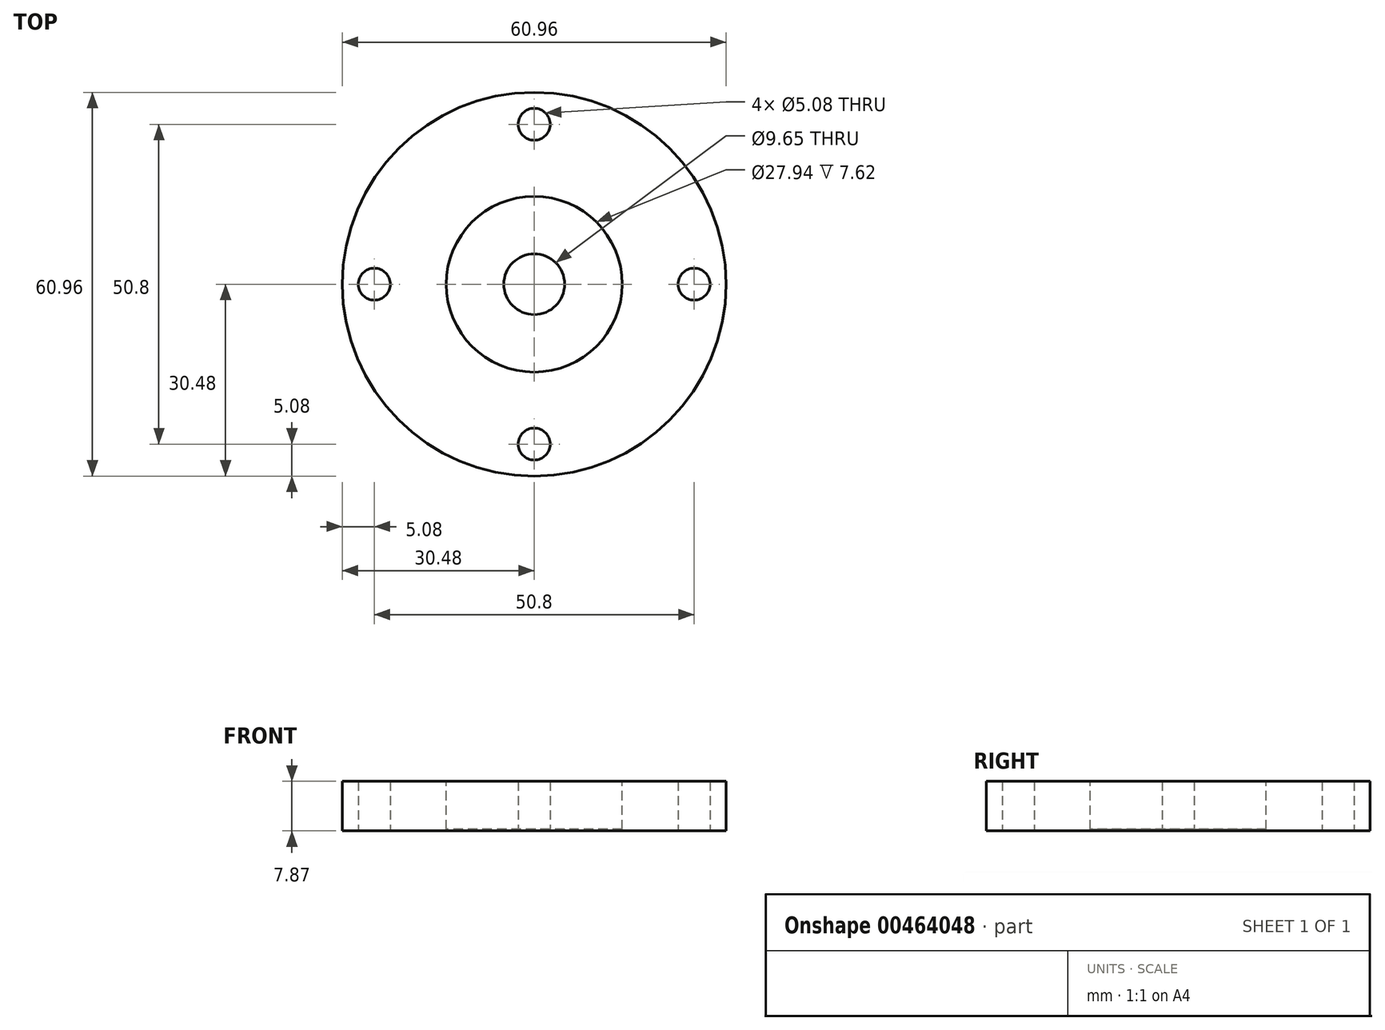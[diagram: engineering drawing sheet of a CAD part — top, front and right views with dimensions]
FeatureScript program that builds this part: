
annotation { "Feature Type Name" : "Feature", "Feature Type Description" : "" }
export const myFeature = defineFeature(function(context is Context, id is Id, definition is map)
    precondition{}
    {
        {
            var Q0;
            Q0=qCreatedBy(makeId("Top.planeOp"),FACE);
            var sketch = newSketch(context, id + "F0", { "sketchPlane" : qUnion([Q0])});
            skCircle(sketch, "E0", {"center": v(0, 0) * mm, "radius": 30.48 * mm});
            skCircle(sketch, "E1", {"center": v(0, 0) * mm, "radius": 4.83 * mm});
            skCircle(sketch, "E2", {"center": v(0, 0) * mm, "radius": 25.4 * mm, "construction": true});
            skCircle(sketch, "E3", {"center": v(-25.4, 0) * mm, "radius": 2.54 * mm});
            skCircle(sketch, "E4.1.0", {"center": v(0, -25.4) * mm, "radius": 2.54 * mm});
            skCircle(sketch, "E4.2.0", {"center": v(25.4, 0) * mm, "radius": 2.54 * mm});
            skCircle(sketch, "E4.3.0", {"center": v(0, 25.4) * mm, "radius": 2.54 * mm});
            skSolve(sketch);
        }
        {
            var Q0;
            Q0=makeQuery(id+"F0.imprint","IMPRINT",FACE,{"disambiguationData":[TD([[makeQuery(id+"F0.imprint","IMPRINT",EDGE,{"derivedFrom":sQuery(id+"F0.wireOp",EDGE,"E0")}),1.0]])]});
            extrude(context, id + "F1", {"entities" : qUnion([Q0]), "depth" : 7.87 * mm, "offsetDistance" : 25.4 * mm});
        }
        {
            var Q0;
            Q0=makeQuery(id+"F1.opExtrude","CAP_FACE",FACE,{"disambiguationData":[OSD([sQuery(id+"F0.wireOp",EDGE,"E0"),sQuery(id+"F0.wireOp",EDGE,"E1"),sQuery(id+"F0.wireOp",EDGE,"E3"),sQuery(id+"F0.wireOp",EDGE,"E4.1.0"),sQuery(id+"F0.wireOp",EDGE,"E4.2.0"),sQuery(id+"F0.wireOp",EDGE,"E4.3.0")])],"isStart":false});
            var sketch = newSketch(context, id + "F2", { "sketchPlane" : qUnion([Q0])});
            skCircle(sketch, "E5", {"center": v(0, 0) * mm, "radius": 13.97 * mm});
            skSolve(sketch);
        }
        {
            var Q0;
            Q0=makeQuery(id+"F2.imprint","IMPRINT",FACE,{"disambiguationData":[TD([[makeQuery(id+"F2.imprint","IMPRINT",EDGE,{"derivedFrom":sQuery(id+"F2.wireOp",EDGE,"E5")}),1.0]])]});
            extrude(context, id + "F3", {"entities" : qUnion([Q0]), "operationType" : NewBodyOperationType.REMOVE, "oppositeDirection" : true, "depth" : 7.62 * mm, "offsetDistance" : 25.4 * mm});
        }
    });
